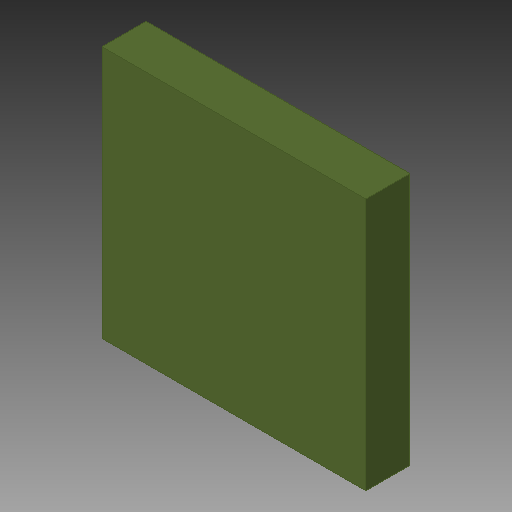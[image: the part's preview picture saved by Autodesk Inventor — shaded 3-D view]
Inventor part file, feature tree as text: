
AUTODESK INVENTOR PART (.ipt)
format: ipt  version: 2018 (Build 220112000, 112)  size: 80,896 bytes
history: native  units: in
note: dims shown in document units (in); Inventor stores cm internally (conversion verified against a paired STEP export)
features: other x1, extrude x1
ambient origin geometry x8: Origin, YZ Plane, XZ Plane, XY Plane, X Axis, Y Axis, Z Axis, Center Point
bodies: Solid1 (feature_tree)
feature tree (2):
  other  "RHB_S-PQFP-N32, TUSB2046BIRHBIRHB_49"
  extrude  "Extrusion1"  Depth=0.0394in TaperAngle=0.0deg
